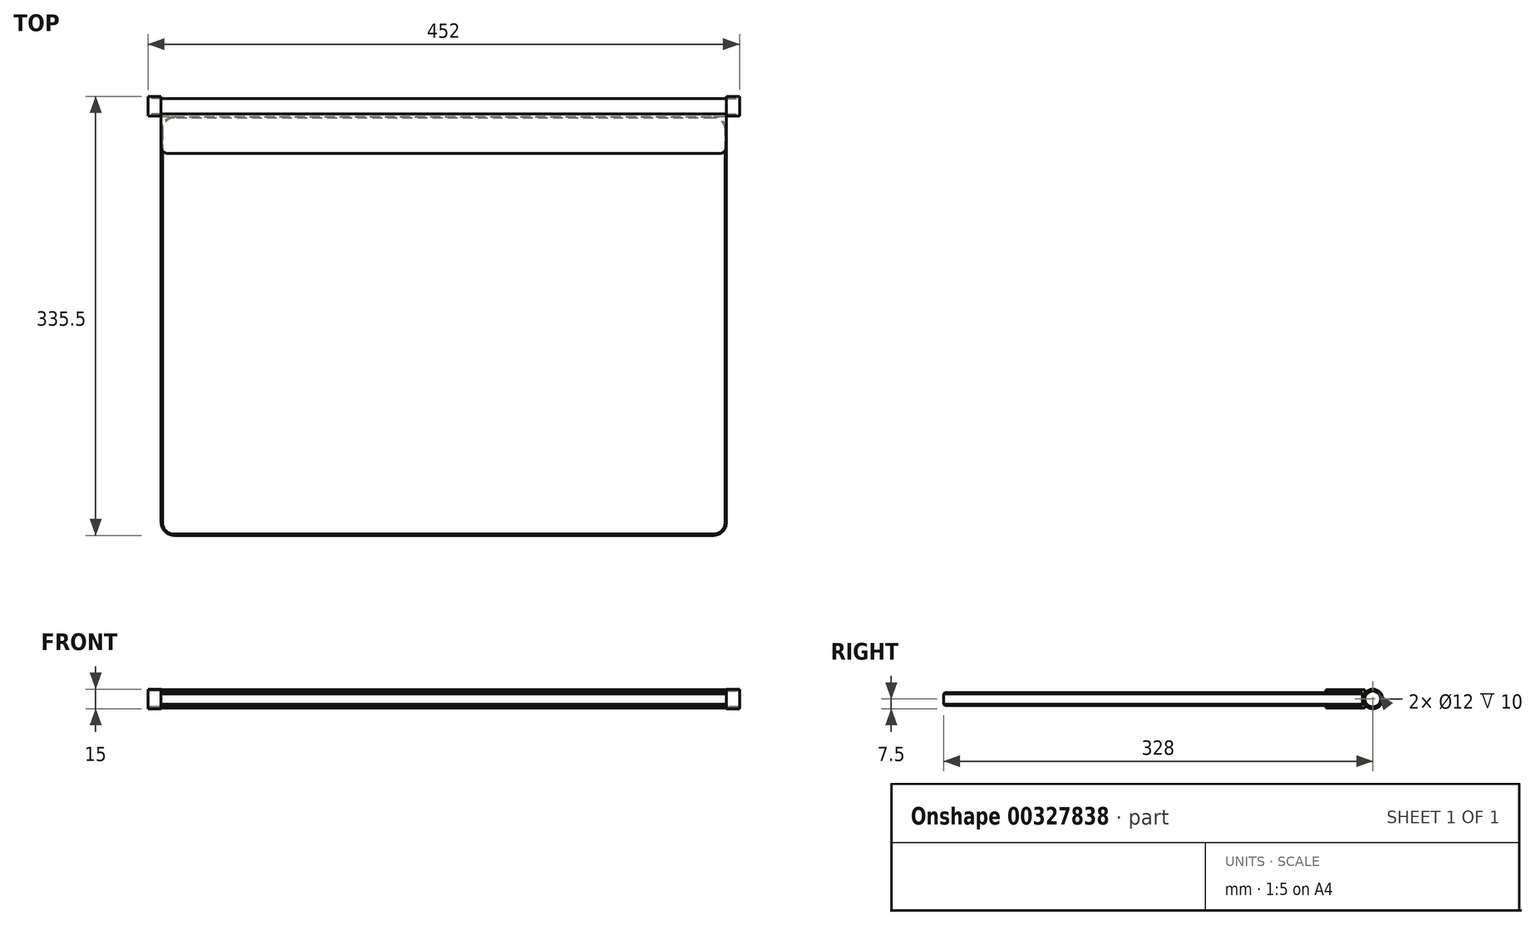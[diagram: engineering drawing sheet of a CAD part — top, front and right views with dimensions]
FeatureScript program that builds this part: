
annotation { "Feature Type Name" : "Feature", "Feature Type Description" : "" }
export const myFeature = defineFeature(function(context is Context, id is Id, definition is map)
    precondition{}
    {
        {
            var Q0;
            Q0=qCreatedBy(makeId("Top.planeOp"),FACE);
            var sketch = newSketch(context, id + "F0", { "sketchPlane" : qUnion([Q0])});
            skLineSegment(sketch, "E0.bottom", {"start": v(-216, -160) * mm, "end": v(216, -160) * mm});
            skLineSegment(sketch, "E0.top", {"start": v(-216, 160) * mm, "end": v(216, 160) * mm});
            skLineSegment(sketch, "E0.left", {"start": v(-216, -160) * mm, "end": v(-216, 160) * mm});
            skLineSegment(sketch, "E0.right", {"start": v(216, -160) * mm, "end": v(216, 160) * mm});
            skPoint(sketch, "E0.middle", {"position": v(0, 0) * mm});
            skSolve(sketch);
        }
        {
            var Q0;
            Q0 = qSketchRegion(id + "F0", true);
            extrude(context, id + "F1", {"entities" : qUnion([Q0]), "depth" : 10 * mm});
        }
        {
            var Q0;
            Q0=makeQuery(id+"F1.opExtrude","SWEPT_EDGE",EDGE,{"disambiguationData":[OSD([sQuery(id+"F0.wireOp",EDGE,"E0.bottom"),sQuery(id+"F0.wireOp",EDGE,"E0.right")])]});
            var Q1;
            Q1=makeQuery(id+"F1.opExtrude","SWEPT_EDGE",EDGE,{"disambiguationData":[OSD([sQuery(id+"F0.wireOp",EDGE,"E0.bottom"),sQuery(id+"F0.wireOp",EDGE,"E0.left")])]});
            var Q2;
            Q2=makeQuery(id+"F1.opExtrude","SWEPT_EDGE",EDGE,{"disambiguationData":[OSD([sQuery(id+"F0.wireOp",EDGE,"E0.top"),sQuery(id+"F0.wireOp",EDGE,"E0.right")])]});
            var Q3;
            Q3=makeQuery(id+"F1.opExtrude","SWEPT_EDGE",EDGE,{"disambiguationData":[OSD([sQuery(id+"F0.wireOp",EDGE,"E0.top"),sQuery(id+"F0.wireOp",EDGE,"E0.left")])]});
            fillet(context, id + "F2", {"entities" : qUnion([Q0, Q1, Q2, Q3]), "radius" : 10 * mm, "tangentPropagation" : true, "allowEdgeOverflow" : false});
        }
        {
            var Q0;
            Q0=qCreatedBy(makeId("Right.planeOp"),FACE);
            var sketch = newSketch(context, id + "F3", { "sketchPlane" : qUnion([Q0])});
            skLineSegment(sketch, "E1", {"start": v(132, 10) * mm, "end": v(132, 12) * mm});
            skLineSegment(sketch, "E2", {"start": v(132, 12) * mm, "end": v(162, 12) * mm});
            skLineSegment(sketch, "E3", {"start": v(162, 12) * mm, "end": v(162, -2) * mm});
            skLineSegment(sketch, "E4", {"start": v(162, -2) * mm, "end": v(132, -2) * mm});
            skLineSegment(sketch, "E5", {"start": v(132, -2) * mm, "end": v(132, 0) * mm});
            skLineSegment(sketch, "E6", {"start": v(132, 0) * mm, "end": v(160, 0) * mm});
            skLineSegment(sketch, "E7", {"start": v(160, 0) * mm, "end": v(160, 10) * mm});
            skLineSegment(sketch, "E8", {"start": v(160, 10) * mm, "end": v(132, 10) * mm});
            skSolve(sketch);
        }
        {
            var Q0;
            Q0=makeQuery(id+"F3.imprint","IMPRINT",FACE,{"disambiguationData":[TD([[makeQuery(id+"F3.imprint","IMPRINT",EDGE,{"derivedFrom":sQuery(id+"F3.wireOp",EDGE,"E1")}),-1.0]])]});
            extrude(context, id + "F4", {"entities" : qUnion([Q0]), "endBound" : BoundingType.SYMMETRIC, "depth" : 432 * mm});
        }
        {
            var Q0;
            Q0=qCreatedBy(makeId("Right.planeOp"),FACE);
            var sketch = newSketch(context, id + "F5", { "sketchPlane" : qUnion([Q0])});
            skCircle(sketch, "E9", {"center": v(168, 5) * mm, "radius": 6 * mm});
            skSolve(sketch);
        }
        {
            var Q0;
            Q0=makeQuery(id+"F5.imprint","IMPRINT",FACE,{"disambiguationData":[TD([[makeQuery(id+"F5.imprint","IMPRINT",EDGE,{"derivedFrom":sQuery(id+"F5.wireOp",EDGE,"E9")}),1.0]])]});
            extrude(context, id + "F6", {"entities" : qUnion([Q0]), "endBound" : BoundingType.SYMMETRIC, "depth" : 452 * mm});
        }
        {
            var Q0;
            Q0=makeQuery(id+"F6.opExtrude","CAP_FACE",FACE,{"disambiguationData":[OSD([sQuery(id+"F5.wireOp",EDGE,"E9")])],"isStart":false});
            var sketch = newSketch(context, id + "F7", { "sketchPlane" : qUnion([Q0])});
            skCircle(sketch, "E10", {"center": v(168, 5) * mm, "radius": 7.5 * mm});
            skCircle(sketch, "E11", {"center": v(168, 5) * mm, "radius": 6 * mm});
            skSolve(sketch);
        }
        {
            var Q0;
            Q0 = qSketchRegion(id + "F7", true);
            extrude(context, id + "F8", {"entities" : qUnion([Q0]), "oppositeDirection" : true, "depth" : 10 * mm});
        }
        {
            var Q0;
            Q0=makeQuery(id+"F8.opExtrude","SWEPT_BODY",BODY,{"disambiguationData":[OSD([sQuery(id+"F7.wireOp",EDGE,"E10"),sQuery(id+"F7.wireOp",EDGE,"E11")])]});
            var Q1;
            Q1=qCreatedBy(makeId("Right.planeOp"),FACE);
            mirror(context, id + "F9", {"entities" : qUnion([Q0]), "mirrorPlane" : qUnion([Q1])});
        }
        {
            var Q0;
            Q0=makeQuery(id+"F1.opExtrude","CAP_FACE",FACE,{"disambiguationData":[OSD([sQuery(id+"F0.wireOp",EDGE,"E0.bottom"),sQuery(id+"F0.wireOp",EDGE,"E0.top"),sQuery(id+"F0.wireOp",EDGE,"E0.left"),sQuery(id+"F0.wireOp",EDGE,"E0.right")])],"isStart":false});
            var Q1;
            Q1=makeQuery(id+"F1.opExtrude","CAP_FACE",FACE,{"disambiguationData":[OSD([sQuery(id+"F0.wireOp",EDGE,"E0.bottom"),sQuery(id+"F0.wireOp",EDGE,"E0.top"),sQuery(id+"F0.wireOp",EDGE,"E0.left"),sQuery(id+"F0.wireOp",EDGE,"E0.right")])],"isStart":true});
            chamfer(context, id + "F10", {"entities" : qUnion([Q0, Q1]), "width" : 1 * mm, "tangentPropagation" : true});
        }
        {
            var Q0;
            Q0=makeQuery(id+"F4.opExtrude","CAP_EDGE",EDGE,{"disambiguationData":[OSD([sQuery(id+"F3.wireOp",EDGE,"E1")])],"isStart":true});
            var Q1;
            Q1=makeQuery(id+"F4.opExtrude","CAP_EDGE",EDGE,{"disambiguationData":[OSD([sQuery(id+"F3.wireOp",EDGE,"E5")])],"isStart":true});
            var Q2;
            Q2=makeQuery(id+"F4.opExtrude","CAP_EDGE",EDGE,{"disambiguationData":[OSD([sQuery(id+"F3.wireOp",EDGE,"E1")])],"isStart":false});
            var Q3;
            Q3=makeQuery(id+"F4.opExtrude","CAP_EDGE",EDGE,{"disambiguationData":[OSD([sQuery(id+"F3.wireOp",EDGE,"E5")])],"isStart":false});
            fillet(context, id + "F11", {"entities" : qUnion([Q0, Q1, Q2, Q3]), "radius" : 5 * mm, "tangentPropagation" : true, "allowEdgeOverflow" : false});
        }
    });
